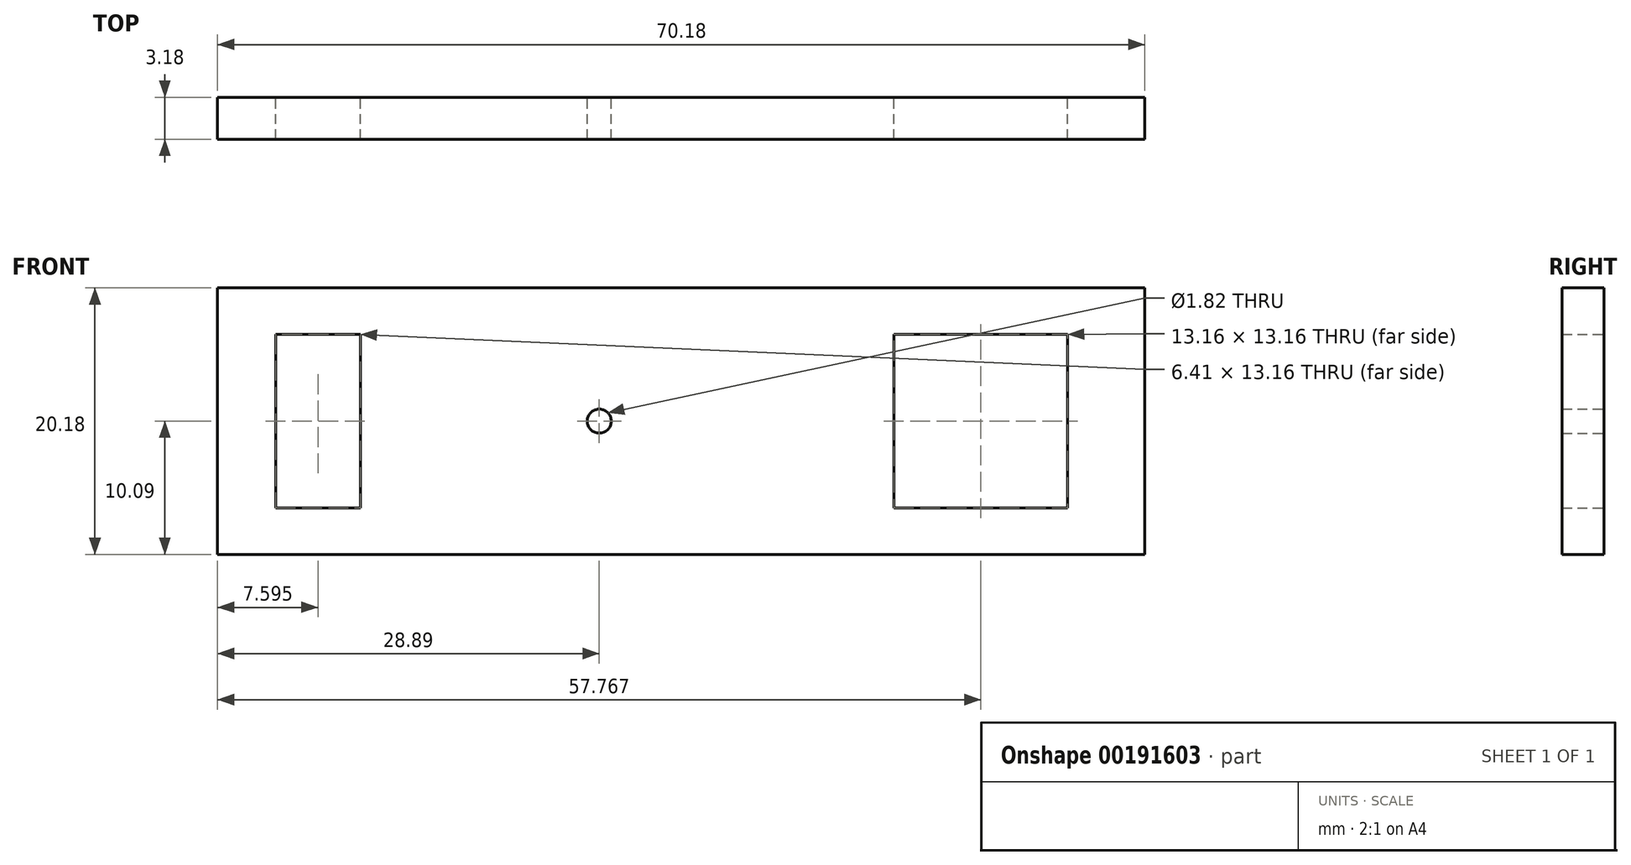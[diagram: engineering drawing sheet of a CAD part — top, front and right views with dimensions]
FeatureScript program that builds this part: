
annotation { "Feature Type Name" : "Feature", "Feature Type Description" : "" }
export const myFeature = defineFeature(function(context is Context, id is Id, definition is map)
    precondition{}
    {
        {
            var Q0;
            Q0=qCreatedBy(makeId("Front.planeOp"),FACE);
            var sketch = newSketch(context, id + "F0", { "sketchPlane" : qUnion([Q0])});
            skLineSegment(sketch, "E0", {"start": v(16.1, 6.58) * mm, "end": v(16.1, -6.58) * mm});
            skLineSegment(sketch, "E1", {"start": v(29.26, 6.58) * mm, "end": v(16.1, 6.58) * mm});
            skLineSegment(sketch, "E2", {"start": v(29.26, -6.58) * mm, "end": v(29.26, 6.58) * mm});
            skLineSegment(sketch, "E3", {"start": v(16.1, -6.58) * mm, "end": v(29.26, -6.58) * mm});
            skLineSegment(sketch, "E4", {"start": v(35.09, -10.09) * mm, "end": v(35.09, 10.09) * mm});
            skLineSegment(sketch, "E5", {"start": v(35.09, 10.09) * mm, "end": v(-35.09, 10.09) * mm});
            skLineSegment(sketch, "E6", {"start": v(-35.09, 10.09) * mm, "end": v(-35.09, -10.09) * mm});
            skLineSegment(sketch, "E7", {"start": v(-35.09, -10.09) * mm, "end": v(35.09, -10.09) * mm});
            skLineSegment(sketch, "E8", {"start": v(-24.29, -6.58) * mm, "end": v(-24.29, 6.58) * mm});
            skLineSegment(sketch, "E9", {"start": v(-30.7, -6.58) * mm, "end": v(-24.29, -6.58) * mm});
            skLineSegment(sketch, "E10", {"start": v(-30.7, 6.58) * mm, "end": v(-30.7, -6.58) * mm});
            skLineSegment(sketch, "E11", {"start": v(-24.29, 6.58) * mm, "end": v(-30.7, 6.58) * mm});
            skCircle(sketch, "E12", {"center": v(-6.2, 0) * mm, "radius": 0.91 * mm});
            skSolve(sketch);
        }
        {
            var Q0;
            Q0=makeQuery(id+"F0.imprint","IMPRINT",FACE,{"disambiguationData":[TD([[makeQuery(id+"F0.imprint","IMPRINT",EDGE,{"derivedFrom":sQuery(id+"F0.wireOp",EDGE,"E0")}),-1.0]])]});
            extrude(context, id + "F1", {"entities" : qUnion([Q0]), "depth" : 3.17 * mm});
        }
    });
